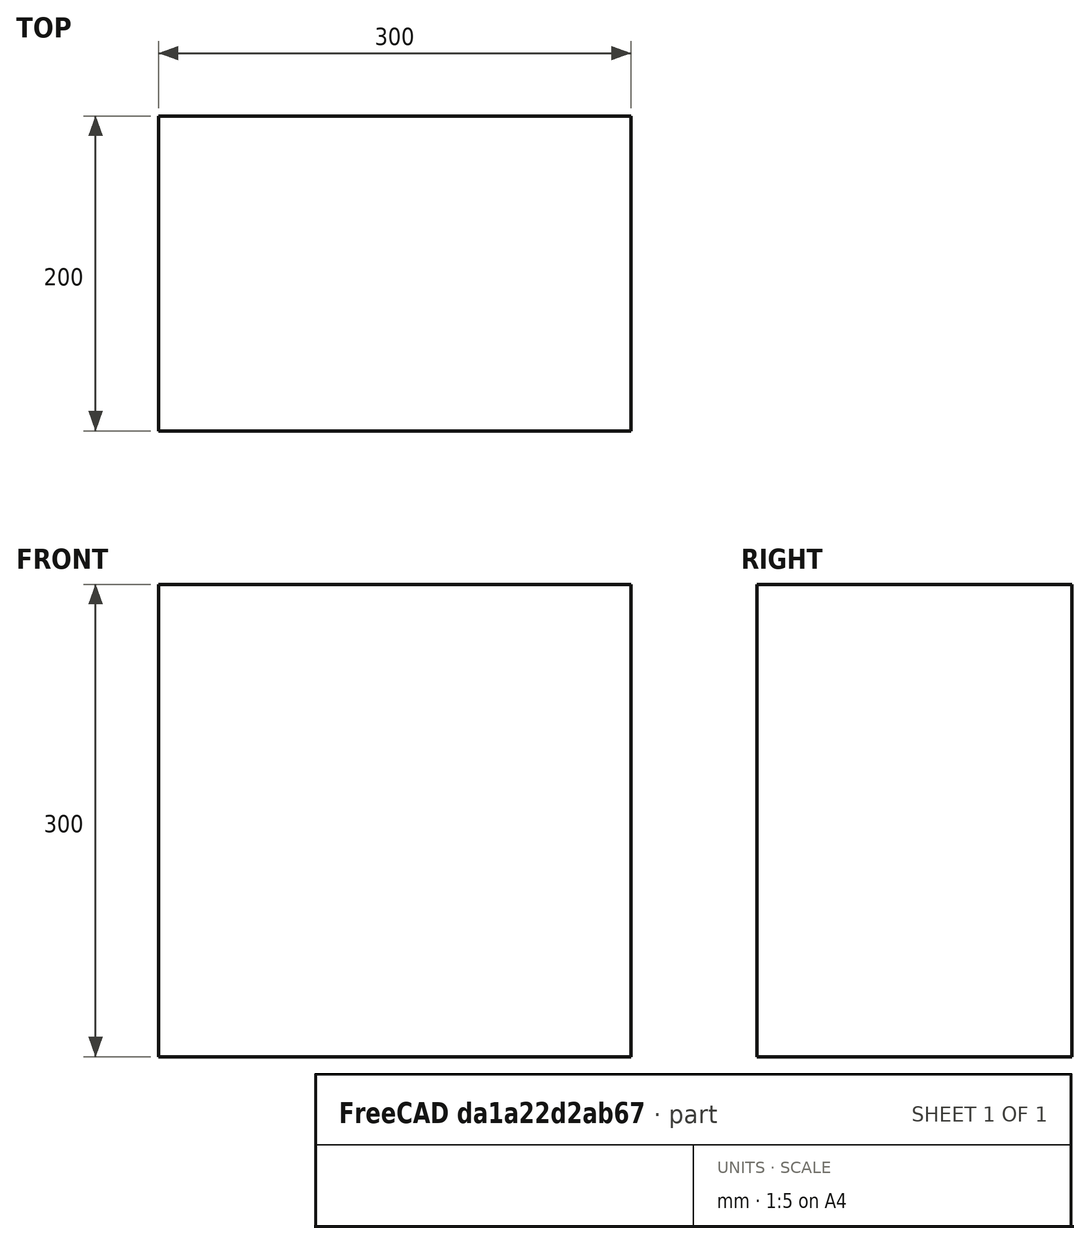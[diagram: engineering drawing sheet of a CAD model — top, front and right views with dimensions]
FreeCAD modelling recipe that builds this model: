
FCSTD DOCUMENT  (FreeCAD 0.19R24291 (Git))
Label: Enclosure
License: All rights reserved
LicenseURL: http://en.wikipedia.org/wiki/All_rights_reserved
objects: Sketcher::SketchObject×2, PartDesign::Pad×1, PartDesign::Body×1
note: 5 computed .brp shape members not serialized (recipe doc carries the construction recipe); baked Part::Feature solids carry a one-line shape summary decoded from their .brp

FEATURE [Sketcher::SketchObject] Sketch
  FullyConstrained = true
  MapMode = 5
  Support = -> [XY_Plane]
  sketch-geometry (4):
    g0: LineSegment StartX=-150 StartY=100 StartZ=0 EndX=150 EndY=100 EndZ=0
    g1: LineSegment StartX=150 StartY=100 StartZ=0 EndX=150 EndY=-100 EndZ=0
    g2: LineSegment StartX=150 StartY=-100 StartZ=0 EndX=-150 EndY=-100 EndZ=0
    g3: LineSegment StartX=-150 StartY=-100 StartZ=0 EndX=-150 EndY=100 EndZ=0
  constraints (12):
    c: Coincident(g0,g1)
    c: Coincident(g1,g2)
    c: Coincident(g2,g3)
    c: Coincident(g3,g0)
    c: Horizontal(g0)
    c: Horizontal(g2)
    c: Vertical(g1)
    c: Vertical(g3)
    c: DistanceY(g3,g3) = 200
    c: DistanceX(g0,g0) = 300
    c: Distance(g-1,g0) = 100
    c: Distance(g-1,g3) = 150
FEATURE [PartDesign::Pad] Pad
  Direction = (1,1,1)
  Length = 300
  Length2 = 100
  Profile = -> Sketch
  Type = 0
FEATURE [Sketcher::SketchObject] Sketch001
  FullyConstrained = true
  MapMode = 5
  Placement = pos=(0,-100,0) rot=(1,0,0;1.5708rad)
  Support = -> [Pad]
FEATURE [PartDesign::Body] Body
  Group = -> [Sketch,Pad,Sketch001]
  Origin = -> Origin
  Tip = -> Pad
